# Revit family: UHRF124-WS01A
name_source: partatom
category: Specialty Equipment
revit_build: Autodesk Revit 2017 (Build: 20160225_1515(x64)
units: mm (PartAtom-declared; Revit-internal decimal feet)

## family parameters
Always vertical = Yes
Cut with Voids When Loaded = No
Part Type = Normal
Room Calculation Point = No
Round Connector Dimension = Use Diameter
Shared = No
Work Plane-Based = No

## types (1)
- UHRF124-WS01A
    Depth = 22 15/16"
    Description = 24” Refrigerator / Freezer
    Door Swing = Field Reversible
    Features and specifications = Freezer volume of 1.5 cu ft
    Finish = White Solid
    Height = 33 11/16"
    Lock = No
    Manufacturer = U-LINE
    Model = UHRF124-WS01A
    Pump = No
    Temperature range = 34 F - 45 F
    Type Comments = Volume of 4.2 cu ft holds up to 61 bottles (12 oz) or 114 cans (12 oz)
    U-Adjust interior = Three removable tempered glass shelves
    URL = https://www.yepsketch.com
    Voltage/Hz = 115 v / 60 hz
    Width = 23 15/16"
    shipping weight = 123 lb

## geometry (parser evidence)
native form markers: Sweep x2
no freeform markers — native parametric forms only
